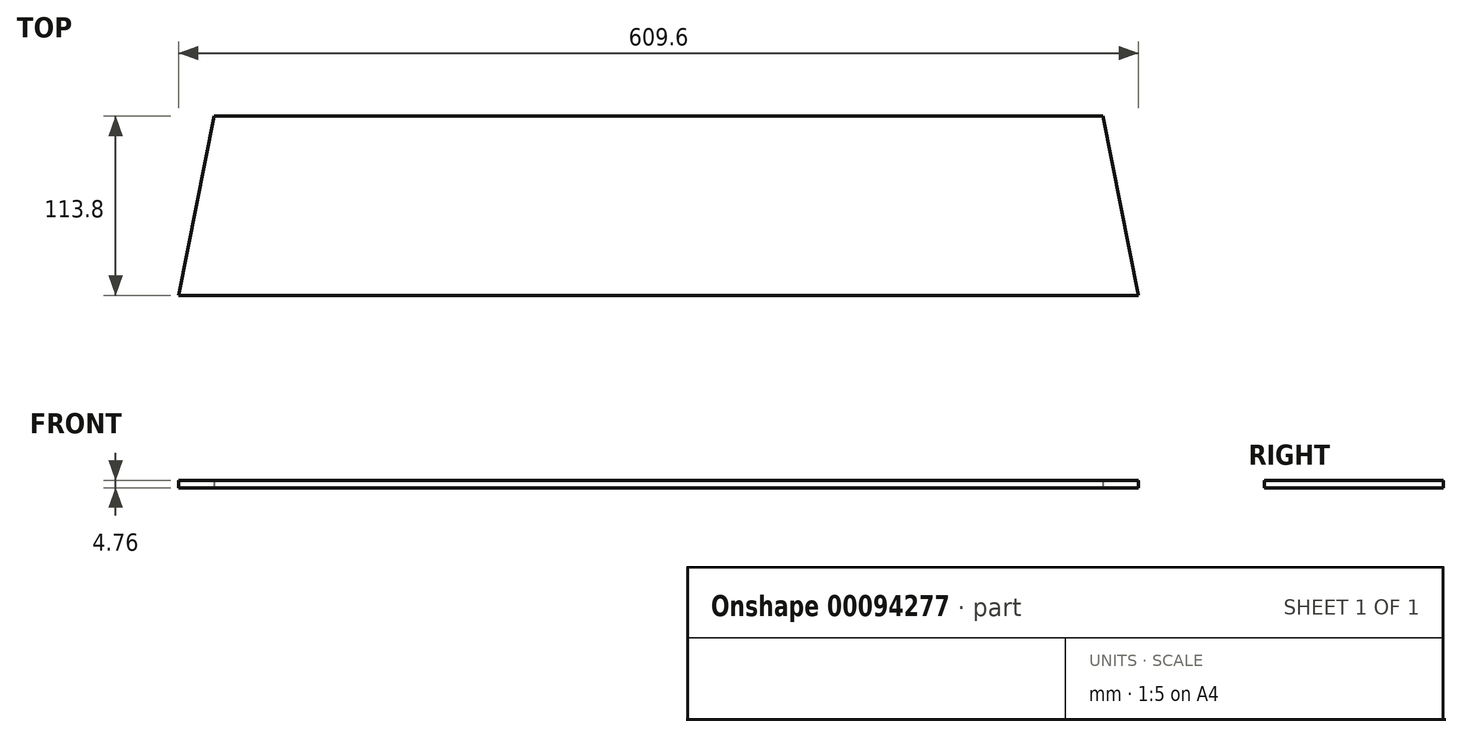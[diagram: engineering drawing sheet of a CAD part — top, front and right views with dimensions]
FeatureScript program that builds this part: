
annotation { "Feature Type Name" : "Feature", "Feature Type Description" : "" }
export const myFeature = defineFeature(function(context is Context, id is Id, definition is map)
    precondition{}
    {
        {
            var Q0;
            Q0=qCreatedBy(makeId("Top.planeOp"),FACE);
            var sketch = newSketch(context, id + "F0", { "sketchPlane" : qUnion([Q0])});
            skLineSegment(sketch, "E0.bottom", {"start": v(314.1, 56.9) * mm, "end": v(-250.7, 56.9) * mm});
            skLineSegment(sketch, "E0.top", {"start": v(336.5, -56.9) * mm, "end": v(-273.1, -56.9) * mm});
            skPoint(sketch, "E0.middle", {"position": v(0, 0) * mm});
            skLineSegment(sketch, "E1", {"start": v(-273.1, -56.9) * mm, "end": v(-250.7, 56.9) * mm});
            skLineSegment(sketch, "E2", {"start": v(336.5, -56.9) * mm, "end": v(314.1, 56.9) * mm});
            skPoint(sketch, "E0.right.start.orphan", {"position": v(-336.5, 56.9) * mm});
            skPoint(sketch, "E0.left.start.orphan", {"position": v(273.1, 56.9) * mm});
            skSolve(sketch);
        }
        {
            var Q0;
            Q0 = qSketchRegion(id + "F0", true);
            extrude(context, id + "F1", {"entities" : qUnion([Q0]), "depth" : 4.76 * mm});
        }
    });
